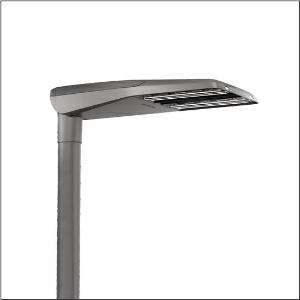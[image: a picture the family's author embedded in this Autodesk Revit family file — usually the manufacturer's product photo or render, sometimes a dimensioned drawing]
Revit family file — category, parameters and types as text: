
# Revit family: streetlight_sl_11_iq_midi___st1_0a_5xc3m51f08le_689c
name_source: partatom
category: Lighting Fixtures
units: mm (PartAtom-declared; Revit-internal decimal feet)

## family parameters
Cut with Voids When Loaded = No
Host = Face
Light Source = No
Part Type = Normal
Room Calculation Point = No
Round Connector Dimension = Use Diameter
Shared = No

## types (1)
- --- (1 x LED, 8920 lm, 60.4 W, 3000K)
    Apparent Load = 60 VA
    CIE Flux Codes = 33 66 96 100 100
    Color Rendering = 70
    Color Temperature = 3000K
    Default Elevation = 1800 mm
    Description = Streetlight SL 11 iQ midi, mast luminaire, primary light control with 3 zone facetted reflector, of plastic, silver coated, highly specular, primary optical cover: cover, of PMMA, transparent, light distribution: ST1.0a, light emission: direct distribution, primary light characteristic: asymmetric, installation type: post-top, side-entry, LED, High Power LED, rated luminous flux: 8.920lm, luminous efficacy: 148lm/W, light colour: 730, colour temperature: 3000K, control: optimised constant luminous flux control (CLO 2.0), Street-Remote, Desk-Remote (wireless, voltage-free reading and setting of iQ features in the workshop via application-optimized NFC function/RFID function), Light-Fading, Smart-Wire, Night-Set, Lumen-Switch, Temp-Guard, Auto-Match, with cable H07RN-F 5x 1.5mm², mains connection: 230..240V, AC, 50/60Hz, connection cable pre-assembled, cable length: 8,5m, start of lifetime: 60W, end of service life: 63W, reduction: 30W, luminaire housing, of diecast aluminium, powder-coated, Siteco® metallic grey (DB 702S), please order mast flange separately, inclination adjustable without tools: 0°, 5°, 10°, 15° (post-top) | 0°, -5°, -10°, -15° (side-entry), sealing non-destructively replaceable, multi-level sealing system, length: 780mm, width: 376mm, height: 118mm, mast flange for spigot size: 42mm (side-entry): 5XC10008XM4, 60/48mm (side-entry/post-top): 5XC10108XM2, 76/60mm (side-entry/post-top): 5XC10108XM1, equipment: standard, protection rating (complete): IP66, insulation class (complete): insulation class II (safety insulation), certification: CE, ENEC, VDE, impact resistance: IK09, permissible operating ambient temperature for outdoor applications: -25..+50°C, standard-compliant lighting for roads and squares, Environmental Product Declaration (EPD) tested and certified by an independent institute, packaging unit: 1 piece

Light Distribution: ST1.0a
    Height = 118 mm
    Lamp = 1 x LED
    Lamp Light Flux = 8920 lm
    Lamp Power = 60.4 W
    Lamp count = 1
    Length = 780 mm
    Luminous efficacy = 148 lm/W
    Manufacturer = Siteco
    ModVariant = No
    Model = 5XC3M51F08LE
    Number of Poles = 1
    OnlyDefault = Yes
    Power Factor = 1
    Product Name = Streetlight SL 11 iQ midi | ST1.0a
    Product group = mast luminaire | pylon top
    ProductGroupID = 6100
    Protection Class = Protection class II
    Protection Degree = IP 66
    RLX_Detail_Level = 1
    RLX_Emergency_Light_Flux = 0 lm
    RLX_Emergency_Type = 0
    RLX_Emergency_Type_DB = No
    RlxData = <blob elided: 70225 chars, md5=e0f9add1>
    Socket = socket
    Standby Power = 0 W
    System Light Flux = 8920 lm
    System Power = 60 W
    Type Comments = factory setting: luminous flux: 100 % | dim-lin: 254 | 520 mA
    Type Image = l_1005960.jpg
    URL = http://relux.com
    VarID = @adj_020815
    Voltage = 0 V
    Weight = 0.00 kg
    Width = 376 mm

## geometry (parser evidence)
native form markers: Blend x4, Sweep x11
no freeform markers — native parametric forms only
